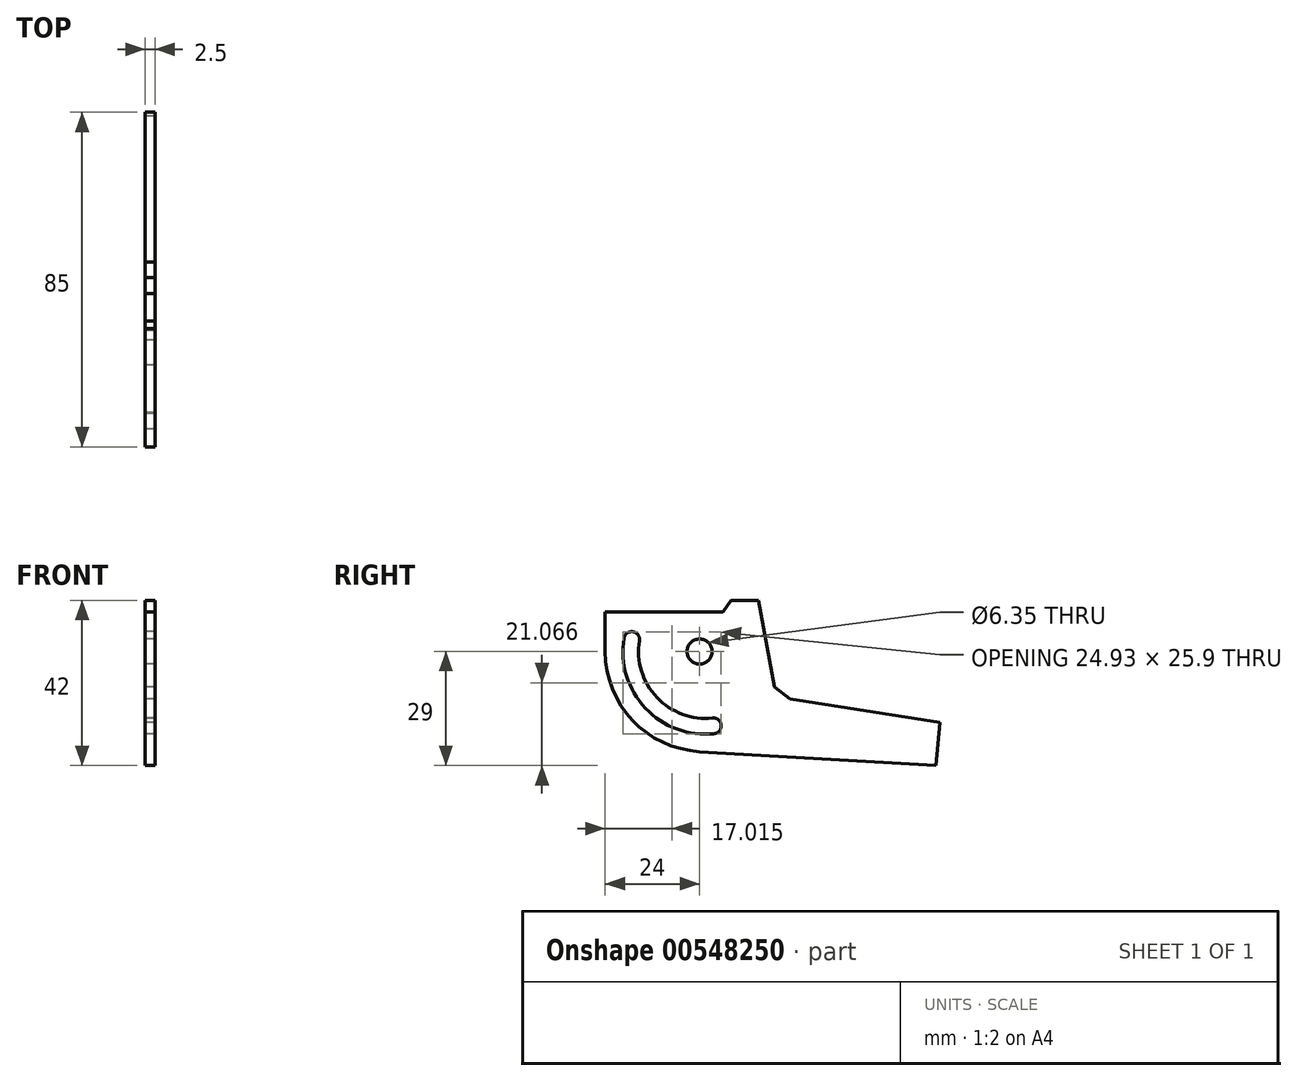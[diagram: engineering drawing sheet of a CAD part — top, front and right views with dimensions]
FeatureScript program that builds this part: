
annotation { "Feature Type Name" : "Feature", "Feature Type Description" : "" }
export const myFeature = defineFeature(function(context is Context, id is Id, definition is map)
    precondition{}
    {
        {
            var Q0;
            Q0=qCreatedBy(makeId("Right.planeOp"),FACE);
            var sketch = newSketch(context, id + "F0", { "sketchPlane" : qUnion([Q0])});
            skLineSegment(sketch, "E0", {"start": v(-24, 0) * mm, "end": v(-24, 10) * mm});
            skLineSegment(sketch, "E1", {"start": v(-24, 10) * mm, "end": v(6, 10) * mm});
            skLineSegment(sketch, "E2", {"start": v(6, 10) * mm, "end": v(8, 13) * mm});
            skLineSegment(sketch, "E3", {"start": v(8, 13) * mm, "end": v(15, 13) * mm});
            skLineSegment(sketch, "E4", {"start": v(15, 13) * mm, "end": v(19, -9) * mm});
            skLineSegment(sketch, "E5", {"start": v(19, -9) * mm, "end": v(23, -12) * mm});
            skArc(sketch, "E6", {"start": v(-24, 0) * mm, "mid": v(-17.05, -17.5) * mm, "end": v(0, -25.46) * mm});
            skLineSegment(sketch, "E7", {"start": v(0, -25.46) * mm, "end": v(60, -29) * mm});
            skLineSegment(sketch, "E8", {"start": v(60, -29) * mm, "end": v(61, -18) * mm});
            skLineSegment(sketch, "E9", {"start": v(61, -18) * mm, "end": v(23, -12) * mm});
            skArc(sketch, "E10", {"start": v(-15.28, 2.72) * mm, "mid": v(-16.93, 5.02) * mm, "end": v(-19.23, 3.36) * mm});
            skArc(sketch, "E11", {"start": v(-19.23, 3.36) * mm, "mid": v(-13.76, -14.43) * mm, "end": v(3.7, -20.88) * mm});
            skArc(sketch, "E12", {"start": v(-15.28, 2.72) * mm, "mid": v(-10.85, -11.68) * mm, "end": v(3.28, -16.9) * mm});
            skArc(sketch, "E13", {"start": v(3.7, -20.88) * mm, "mid": v(5.48, -18.69) * mm, "end": v(3.28, -16.9) * mm});
            skPoint(sketch, "E13.third.point", {"position": v(5.1, -17.71) * mm});
            skLineSegment(sketch, "E14", {"start": v(1.5, 0) * mm, "end": v(1.5, -13.63) * mm, "construction": true});
            skLineSegment(sketch, "E15", {"start": v(1.5, 0) * mm, "end": v(3.49, -18.9) * mm, "construction": true});
            skLineSegment(sketch, "E16", {"start": v(0, 0) * mm, "end": v(-12.25, 0) * mm, "construction": true});
            skLineSegment(sketch, "E17", {"start": v(-17.25, 3.04) * mm, "end": v(0, 0) * mm, "construction": true});
            skCircle(sketch, "E18", {"center": v(0, 0) * mm, "radius": 3.17 * mm});
            skSolve(sketch);
        }
        {
            var Q0;
            Q0=makeQuery(id+"F0.imprint","IMPRINT",FACE,{"disambiguationData":[TD([[makeQuery(id+"F0.imprint","IMPRINT",EDGE,{"derivedFrom":sQuery(id+"F0.wireOp",EDGE,"E0")}),-1.0]])]});
            extrude(context, id + "F1", {"entities" : qUnion([Q0]), "endBound" : BoundingType.SYMMETRIC, "depth" : 2.5 * mm, "offsetDistance" : 25 * mm});
        }
    });
